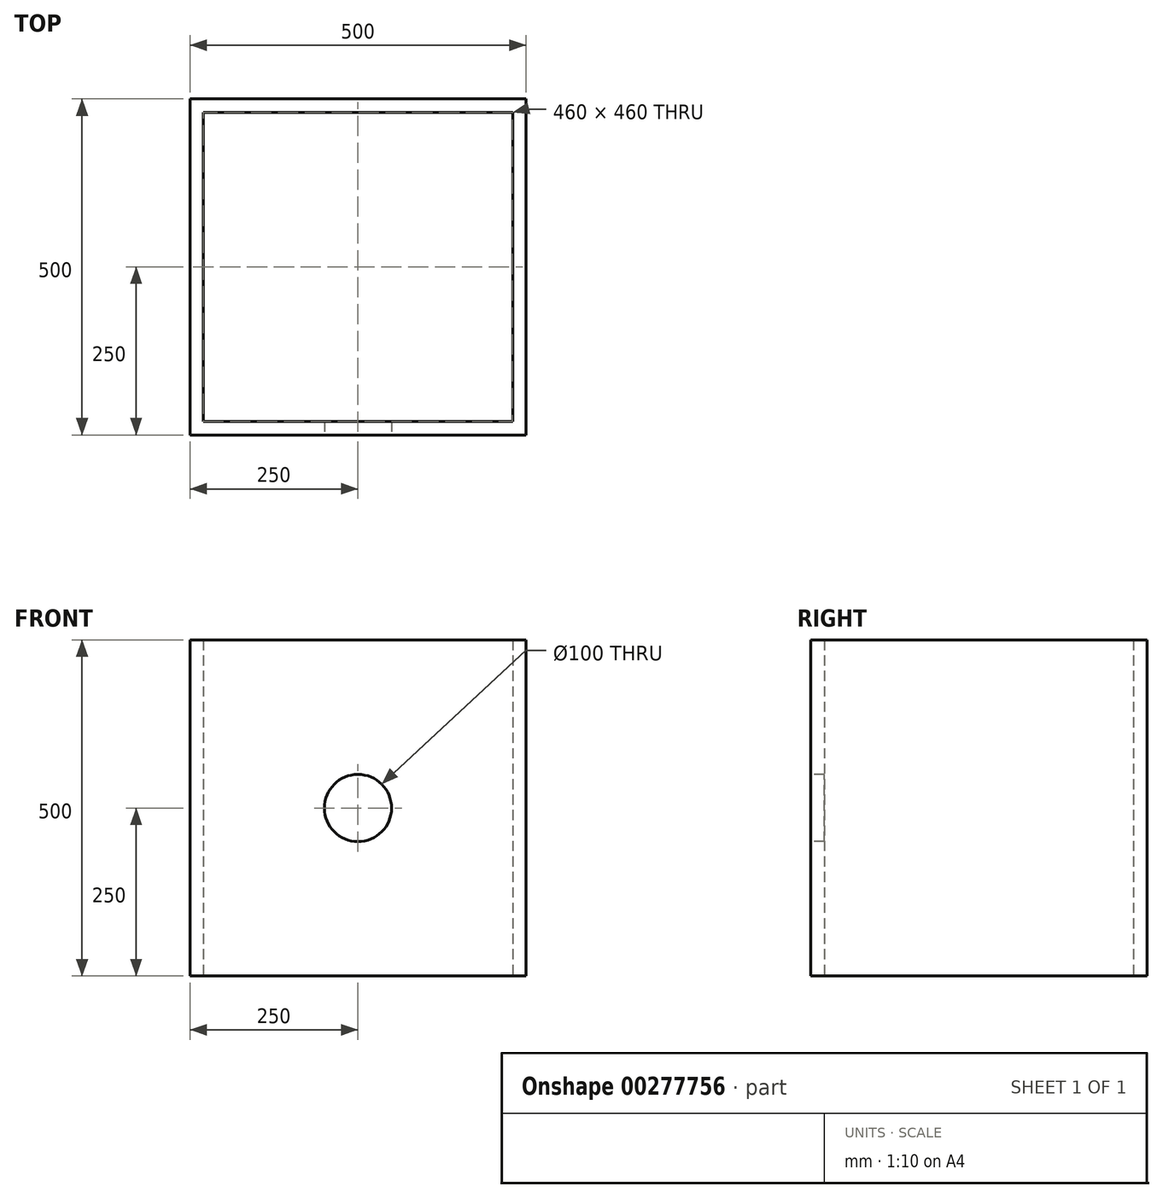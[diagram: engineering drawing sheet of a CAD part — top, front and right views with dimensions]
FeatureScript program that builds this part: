
annotation { "Feature Type Name" : "Feature", "Feature Type Description" : "" }
export const myFeature = defineFeature(function(context is Context, id is Id, definition is map)
    precondition{}
    {
        {
            var Q0;
            Q0=qCreatedBy(makeId("Top.planeOp"),FACE);
            var sketch = newSketch(context, id + "F0", { "sketchPlane" : qUnion([Q0])});
            skLineSegment(sketch, "E0.bottom", {"start": v(250, 250) * mm, "end": v(-250, 250) * mm});
            skLineSegment(sketch, "E0.top", {"start": v(250, -250) * mm, "end": v(-250, -250) * mm});
            skLineSegment(sketch, "E0.left", {"start": v(250, 250) * mm, "end": v(250, -250) * mm});
            skLineSegment(sketch, "E0.right", {"start": v(-250, 250) * mm, "end": v(-250, -250) * mm});
            skPoint(sketch, "E0.middle", {"position": v(0, 0) * mm});
            skLineSegment(sketch, "E1.0", {"start": v(-230, 230) * mm, "end": v(-230, -230) * mm});
            skLineSegment(sketch, "E1.1", {"start": v(230, 230) * mm, "end": v(-230, 230) * mm});
            skLineSegment(sketch, "E1.2", {"start": v(230, 230) * mm, "end": v(230, -230) * mm});
            skLineSegment(sketch, "E1.3", {"start": v(230, -230) * mm, "end": v(-230, -230) * mm});
            skSolve(sketch);
        }
        {
            var Q0;
            Q0 = qSketchRegion(id + "F0", true);
            extrude(context, id + "F1", {"entities" : qUnion([Q0]), "depth" : 500 * mm});
        }
        {
            var Q0;
            Q0=makeQuery(id+"F1.opExtrude","SWEPT_FACE",FACE,{"disambiguationData":[OSD([sQuery(id+"F0.wireOp",EDGE,"E0.top")])]});
            var sketch = newSketch(context, id + "F2", { "sketchPlane" : qUnion([Q0])});
            skCircle(sketch, "E2", {"center": v(0, 250) * mm, "radius": 50 * mm});
            skSolve(sketch);
        }
        {
            var Q0;
            Q0=makeQuery(id+"F2.imprint","IMPRINT",FACE,{"disambiguationData":[TD([[makeQuery(id+"F2.imprint","IMPRINT",EDGE,{"derivedFrom":sQuery(id+"F2.wireOp",EDGE,"E2")}),1.0]])]});
            extrude(context, id + "F3", {"entities" : qUnion([Q0]), "operationType" : NewBodyOperationType.REMOVE, "oppositeDirection" : true, "depth" : 25 * mm});
        }
    });
